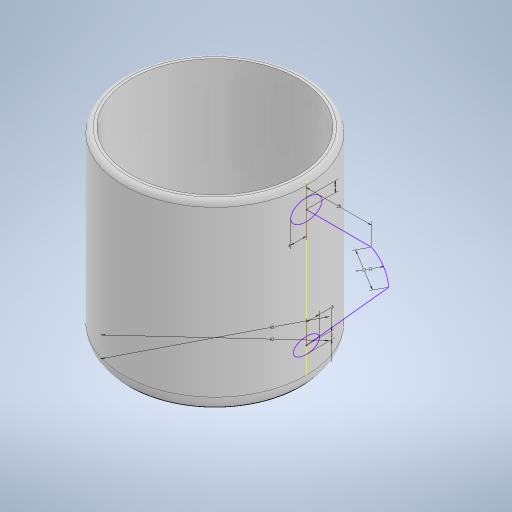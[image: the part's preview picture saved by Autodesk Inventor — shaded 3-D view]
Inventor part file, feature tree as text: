
AUTODESK INVENTOR PART (.ipt)
format: ipt  version: 2024 (Build 280153000, 153)  size: 266,752 bytes
history: native  units: mm
features: sketch x5, other x4, plane x2, revolve x1, shell x1, fillet x1
ambient origin geometry x8: Origin, YZ Plane, XZ Plane, XY Plane, X Axis, Y Axis, Z Axis, Center Point
bodies: Body1 (feature_tree)
feature tree (14):
  other  "Sección transversal1"
  other  "Sólido1"
  revolve  "Revolución1"  [1 undecoded]
  shell  "Vaciado1"  Thickness=35.0mm
  sketch  "Boceto2"  dims[d4=90.0deg]
  other  "Punto de trabajo1"
  plane  "Plano de trabajo1"
  sketch  "Boceto3"  dims[d5=3.0mm]
  other  "Punto de trabajo8"
  plane  "Plano de trabajo10"
  sketch  "Boceto8"  dims[d6=0.5mm d7=2.0mm d8=0.0mm d9=20.0mm]
  fillet  "Empalme1"  Radius=65.0mm
  sketch  "Boceto9"  dims[d10=25.0mm d11=12.0mm d12=12.0mm d14=4.0mm d15=6.0mm d23=5.0mm d24=3.0mm d25=2.0mm d26=65.0mm d27=62.0mm]
  sketch  "Boceto1"  dims[d0=32.5mm d1=70.0mm d2=35.0mm d3=65.0mm]
note: 1 required parameter value undecoded (feature->parameter linkage not recoverable at this tier; creation-order binding heuristic only, values carry confidence <= 0.55)
